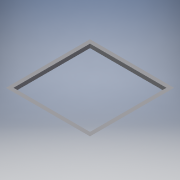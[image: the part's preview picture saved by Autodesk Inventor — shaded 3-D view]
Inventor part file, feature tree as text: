
AUTODESK INVENTOR PART (.ipt)
format: ipt  version: 2018 (Build 220112000, 112)  size: 125,952 bytes
history: native  units: mm
features: reference x13, other x7, extrude x2, sketch x2, chamfer x1, plane x1
ambient origin geometry x8: Origin, YZ Plane, XZ Plane, XY Plane, X Axis, Y Axis, Z Axis, Center Point
bodies: Volumenkörper1 (feature_tree)
feature tree (26):
  extrude  "Extrusion1"  Depth=20.0mm TaperAngle=45.0deg
  chamfer  "Fase1"  Distance=17.0mm
  plane  "Arbeitsebene1"
  extrude  "Extrusion2"  [1 undecoded]
  sketch  "Skizze1"  dims[d0=20.0mm d1=0.0mm d2=20.0mm d3=2.0mm d4=45.0deg]
  reference  "Referenz1"
  reference  "Referenz2"
  reference  "Referenz3"
  reference  "Referenz4"
  reference  "Referenz5"
  sketch  "Skizze3"  dims[d5=-20.0mm d6=17.0mm d7=0.0mm]
  reference  "Referenz12"
  reference  "Referenz13"
  reference  "Referenz14"
  reference  "Referenz15"
  reference  "Referenz16"
  reference  "Referenz17"
  reference  "Referenz18"
  reference  "Referenz19"
  parser-record x1  (decoder bookkeeping rows leaked as tree rows — omitted from the tree; the rows remain in map.json)
  other  "SmartCube_Quadratisch.iam"
  other  "Wand2_MIR:1"
  other  "Wand1:1"
  other  "Wand1_MIR:1"
  other  "Wand2:1"
  other  "PV_Modul:1"
note: 1 required parameter value undecoded (feature->parameter linkage not recoverable at this tier; creation-order binding heuristic only, values carry confidence <= 0.55)
note: 1 file-system path scrubbed to <path> (originals preserved in map.json)
